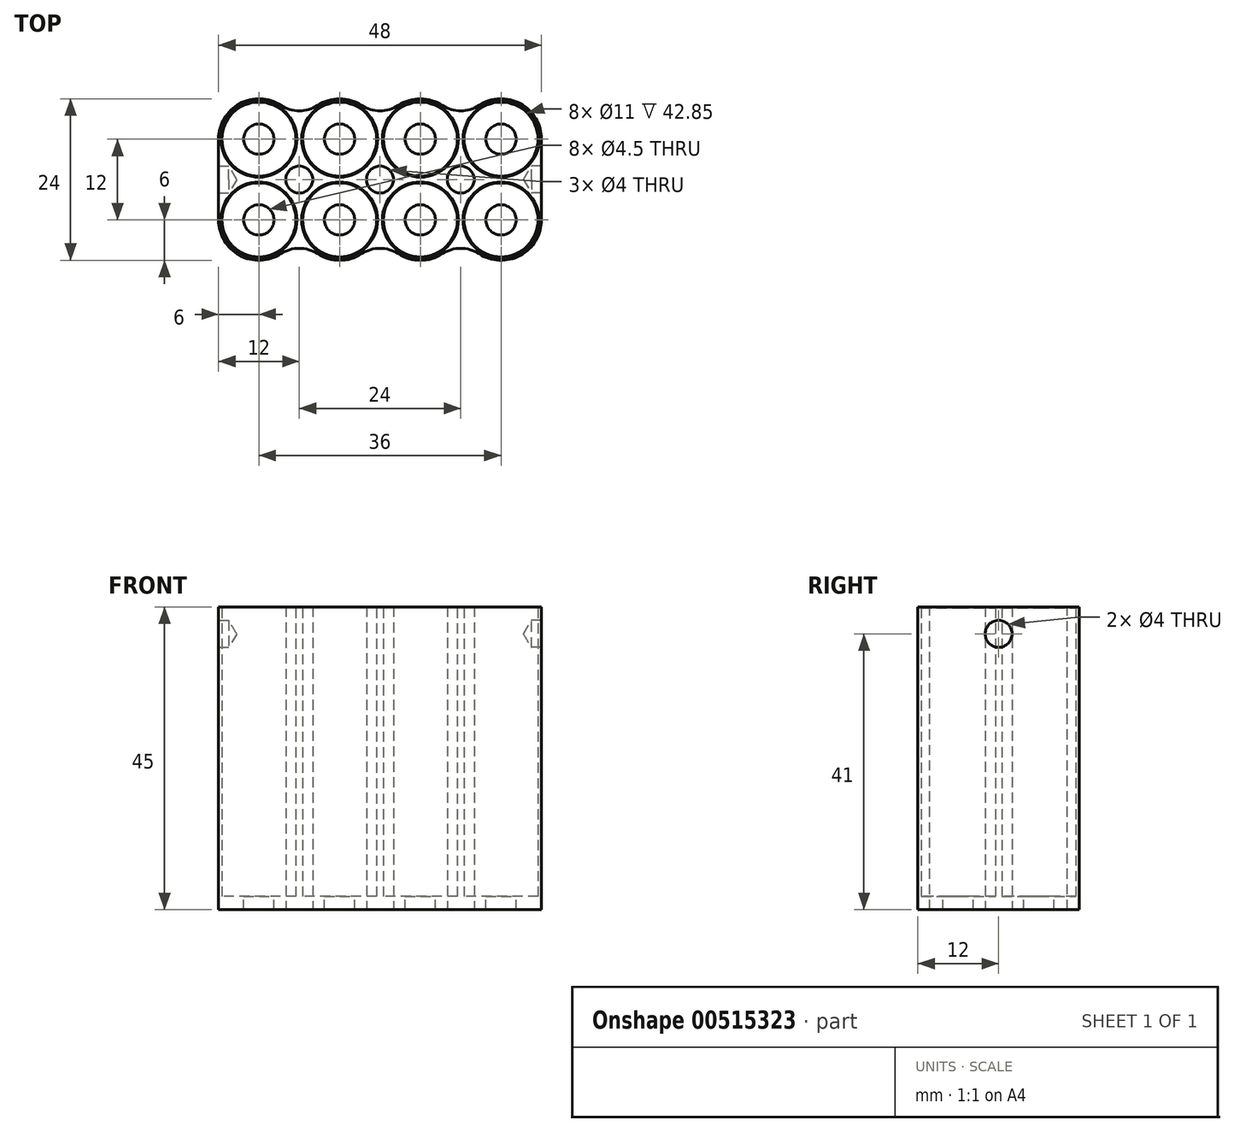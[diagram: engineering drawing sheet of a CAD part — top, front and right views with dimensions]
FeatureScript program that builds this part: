
annotation { "Feature Type Name" : "Feature", "Feature Type Description" : "" }
export const myFeature = defineFeature(function(context is Context, id is Id, definition is map)
    precondition{}
    {
        {
            var Q0;
            Q0=qCreatedBy(makeId("Top.planeOp"),FACE);
            var sketch = newSketch(context, id + "F0", { "sketchPlane" : qUnion([Q0])});
            skCircle(sketch, "E0", {"center": v(-6, 6) * mm, "radius": 5.5 * mm});
            skCircle(sketch, "E1", {"center": v(-18, 6) * mm, "radius": 5.5 * mm});
            skArc(sketch, "E2", {"start": v(-12, 6) * mm, "mid": v(-18, 12) * mm, "end": v(-24, 6) * mm});
            skArc(sketch, "E3", {"start": v(0, 6) * mm, "mid": v(-6, 12) * mm, "end": v(-12, 6) * mm});
            skCircle(sketch, "E4.MirrorC", {"center": v(-6, -6) * mm, "radius": 5.5 * mm});
            skCircle(sketch, "E5.MirrorC", {"center": v(-18, -6) * mm, "radius": 5.5 * mm});
            skArc(sketch, "E6.MirrorCS", {"start": v(0, -6) * mm, "mid": v(-6, -12) * mm, "end": v(-12, -6) * mm});
            skArc(sketch, "E7.MirrorCS", {"start": v(-12, -6) * mm, "mid": v(-18, -12) * mm, "end": v(-24, -6) * mm});
            skCircle(sketch, "E8.MirrorC", {"center": v(18, 6) * mm, "radius": 5.5 * mm});
            skCircle(sketch, "E9.MirrorC", {"center": v(6, -6) * mm, "radius": 5.5 * mm});
            skCircle(sketch, "E10.MirrorC", {"center": v(6, 6) * mm, "radius": 5.5 * mm});
            skArc(sketch, "E11.MirrorCS", {"start": v(0, -6) * mm, "mid": v(6, -12) * mm, "end": v(12, -6) * mm});
            skArc(sketch, "E12.MirrorCS", {"start": v(12, 6) * mm, "mid": v(18, 12) * mm, "end": v(24, 6) * mm});
            skArc(sketch, "E13.MirrorCS", {"start": v(12, -6) * mm, "mid": v(18, -12) * mm, "end": v(24, -6) * mm});
            skCircle(sketch, "E14.MirrorC", {"center": v(18, -6) * mm, "radius": 5.5 * mm});
            skArc(sketch, "E15.MirrorCS", {"start": v(0, 6) * mm, "mid": v(6, 12) * mm, "end": v(12, 6) * mm});
            skCircle(sketch, "E16", {"center": v(-12, 0) * mm, "radius": 2 * mm});
            skCircle(sketch, "E17", {"center": v(0, 0) * mm, "radius": 2 * mm});
            skCircle(sketch, "E18", {"center": v(12, 0) * mm, "radius": 2 * mm});
            skLineSegment(sketch, "E19", {"start": v(-24, 6) * mm, "end": v(-24, -6) * mm});
            skLineSegment(sketch, "E20", {"start": v(24, 6) * mm, "end": v(24, -6) * mm});
            skSolve(sketch);
        }
        {
            var Q0;
            Q0 = qSketchRegion(id + "F0", true);
            extrude(context, id + "F1", {"entities" : qUnion([Q0]), "depth" : 43 * mm, "offsetDistance" : 25 * mm});
        }
        {
            var Q0;
            Q0=makeQuery(id+"F1.opExtrude","CAP_FACE",FACE,{"disambiguationData":[OSD([sQuery(id+"F0.wireOp",EDGE,"E0"),sQuery(id+"F0.wireOp",EDGE,"E1"),sQuery(id+"F0.wireOp",EDGE,"E2"),sQuery(id+"F0.wireOp",EDGE,"E3"),sQuery(id+"F0.wireOp",EDGE,"E4.MirrorC"),sQuery(id+"F0.wireOp",EDGE,"E5.MirrorC"),sQuery(id+"F0.wireOp",EDGE,"E6.MirrorCS"),sQuery(id+"F0.wireOp",EDGE,"E7.MirrorCS"),sQuery(id+"F0.wireOp",EDGE,"E8.MirrorC"),sQuery(id+"F0.wireOp",EDGE,"E9.MirrorC"),sQuery(id+"F0.wireOp",EDGE,"E10.MirrorC"),sQuery(id+"F0.wireOp",EDGE,"E11.MirrorCS"),sQuery(id+"F0.wireOp",EDGE,"E12.MirrorCS"),sQuery(id+"F0.wireOp",EDGE,"E13.MirrorCS"),sQuery(id+"F0.wireOp",EDGE,"E14.MirrorC"),sQuery(id+"F0.wireOp",EDGE,"E15.MirrorCS"),sQuery(id+"F0.wireOp",EDGE,"2cUwnYCC-gtrQ-3R2t-ya3r-G7VDNndyc5e5"),sQuery(id+"F0.wireOp",EDGE,"hSRJbXHy-CsvW-6MMe-1okK-EmNHOIwR2LyR"),sQuery(id+"F0.wireOp",EDGE,"E16"),sQuery(id+"F0.wireOp",EDGE,"E17"),sQuery(id+"F0.wireOp",EDGE,"E18")])],"isStart":true});
            var sketch = newSketch(context, id + "F2", { "sketchPlane" : qUnion([Q0])});
            skArc(sketch, "E21", {"start": v(0, 6) * mm, "mid": v(-6, 12) * mm, "end": v(-12, 6) * mm});
            skArc(sketch, "E22", {"start": v(12, 6) * mm, "mid": v(6, 12) * mm, "end": v(0, 6) * mm});
            skArc(sketch, "E23", {"start": v(-12, -6) * mm, "mid": v(-6, -12) * mm, "end": v(0, -6) * mm});
            skArc(sketch, "E24", {"start": v(0, -6) * mm, "mid": v(6, -12) * mm, "end": v(12, -6) * mm});
            skCircle(sketch, "E25", {"center": v(-6, 6) * mm, "radius": 2.25 * mm});
            skCircle(sketch, "E26", {"center": v(6, 6) * mm, "radius": 2.25 * mm});
            skCircle(sketch, "E27", {"center": v(-6, -6) * mm, "radius": 2.25 * mm});
            skCircle(sketch, "E28", {"center": v(6, -6) * mm, "radius": 2.25 * mm});
            skCircle(sketch, "E29", {"center": v(0, 0) * mm, "radius": 2 * mm});
            skCircle(sketch, "E30", {"center": v(-12, 0) * mm, "radius": 2 * mm});
            skArc(sketch, "E31", {"start": v(12, -6) * mm, "mid": v(18, -12) * mm, "end": v(24, -6) * mm});
            skLineSegment(sketch, "E32", {"start": v(-12, 6) * mm, "end": v(-12, 6) * mm});
            skCircle(sketch, "E33", {"center": v(-18, 6) * mm, "radius": 2.25 * mm});
            skCircle(sketch, "E34", {"center": v(18, -6) * mm, "radius": 2.25 * mm});
            skLineSegment(sketch, "E35", {"start": v(24, -6) * mm, "end": v(24, 6) * mm});
            skArc(sketch, "E36", {"start": v(24, 6) * mm, "mid": v(18, 12) * mm, "end": v(12, 6) * mm});
            skArc(sketch, "E37", {"start": v(-24, -6) * mm, "mid": v(-18, -12) * mm, "end": v(-12, -6) * mm});
            skArc(sketch, "E38", {"start": v(-12, 6) * mm, "mid": v(-18, 12) * mm, "end": v(-24, 6) * mm});
            skLineSegment(sketch, "E39", {"start": v(-24, -6) * mm, "end": v(-24, 6) * mm});
            skCircle(sketch, "E40", {"center": v(-18, -6) * mm, "radius": 2.25 * mm});
            skCircle(sketch, "E41", {"center": v(18, 6) * mm, "radius": 2.25 * mm});
            skCircle(sketch, "E42", {"center": v(12, 0) * mm, "radius": 2 * mm});
            skSolve(sketch);
        }
        {
            var Q0;
            Q0=makeQuery(id+"F1.opExtrude","CAP_EDGE",EDGE,{"disambiguationData":[OSD([sQuery(id+"F0.wireOp",EDGE,"E1")])],"isStart":false});
            var Q1;
            Q1=makeQuery(id+"F1.opExtrude","CAP_EDGE",EDGE,{"disambiguationData":[OSD([sQuery(id+"F0.wireOp",EDGE,"E0")])],"isStart":false});
            var Q2;
            Q2=makeQuery(id+"F1.opExtrude","CAP_EDGE",EDGE,{"disambiguationData":[OSD([sQuery(id+"F0.wireOp",EDGE,"E10.MirrorC")])],"isStart":false});
            var Q3;
            Q3=makeQuery(id+"F1.opExtrude","CAP_EDGE",EDGE,{"disambiguationData":[OSD([sQuery(id+"F0.wireOp",EDGE,"E8.MirrorC")])],"isStart":false});
            var Q4;
            Q4=makeQuery(id+"F1.opExtrude","CAP_EDGE",EDGE,{"disambiguationData":[OSD([sQuery(id+"F0.wireOp",EDGE,"E14.MirrorC")])],"isStart":false});
            var Q5;
            Q5=makeQuery(id+"F1.opExtrude","CAP_EDGE",EDGE,{"disambiguationData":[OSD([sQuery(id+"F0.wireOp",EDGE,"E9.MirrorC")])],"isStart":false});
            var Q6;
            Q6=makeQuery(id+"F1.opExtrude","CAP_EDGE",EDGE,{"disambiguationData":[OSD([sQuery(id+"F0.wireOp",EDGE,"E4.MirrorC")])],"isStart":false});
            var Q7;
            Q7=makeQuery(id+"F1.opExtrude","CAP_EDGE",EDGE,{"disambiguationData":[OSD([sQuery(id+"F0.wireOp",EDGE,"E5.MirrorC")])],"isStart":false});
            chamfer(context, id + "F3", {"entities" : qUnion([Q0, Q1, Q2, Q3, Q4, Q5, Q6, Q7]), "width" : .15 * mm, "tangentPropagation" : true});
        }
        {
            var Q0;
            Q0=makeQuery(id+"F1.opExtrude","SWEPT_FACE",FACE,{"disambiguationData":[OSD([sQuery(id+"F0.wireOp",EDGE,"E19")])]});
            var sketch = newSketch(context, id + "F4", { "sketchPlane" : qUnion([Q0])});
            skPoint(sketch, "E43", {"position": v(0, 39) * mm});
            skSolve(sketch);
        }
        {
            var Q0;
            Q0 = qSketchRegion(id + "F2", true);
            extrude(context, id + "F5", {"entities" : qUnion([Q0]), "operationType" : NewBodyOperationType.ADD, "depth" : 2 * mm, "offsetDistance" : 25 * mm});
        }
        {
            var Q0;
            Q0=makeQuery(id+"F5.boolean.opBoolean","MERGE",EDGE,{"derivedFrom":[makeQuery(id+"F1.opExtrude","SWEPT_EDGE",EDGE,{"disambiguationData":[OSD([sQuery(id+"F0.wireOp",EDGE,"E11.MirrorCS"),sQuery(id+"F0.wireOp",EDGE,"E13.MirrorCS")])]}),makeQuery(id+"F5.opExtrude","SWEPT_EDGE",EDGE,{"disambiguationData":[OSD([sQuery(id+"F2.wireOp",EDGE,"E22"),sQuery(id+"F2.wireOp",EDGE,"E36")])]})]});
            var Q1;
            Q1=makeQuery(id+"F5.boolean.opBoolean","MERGE",EDGE,{"derivedFrom":[makeQuery(id+"F1.opExtrude","SWEPT_EDGE",EDGE,{"disambiguationData":[OSD([sQuery(id+"F0.wireOp",EDGE,"E6.MirrorCS"),sQuery(id+"F0.wireOp",EDGE,"E11.MirrorCS")])]}),makeQuery(id+"F5.opExtrude","SWEPT_EDGE",EDGE,{"disambiguationData":[OSD([sQuery(id+"F2.wireOp",EDGE,"E21"),sQuery(id+"F2.wireOp",EDGE,"E22")])]})]});
            var Q2;
            Q2=makeQuery(id+"F5.boolean.opBoolean","MERGE",EDGE,{"derivedFrom":[makeQuery(id+"F1.opExtrude","SWEPT_EDGE",EDGE,{"disambiguationData":[OSD([sQuery(id+"F0.wireOp",EDGE,"E6.MirrorCS"),sQuery(id+"F0.wireOp",EDGE,"E7.MirrorCS")])]}),makeQuery(id+"F5.opExtrude","SWEPT_EDGE",EDGE,{"disambiguationData":[OSD([sQuery(id+"F2.wireOp",EDGE,"E21"),sQuery(id+"F2.wireOp",EDGE,"E38")])]})]});
            var Q3;
            Q3=makeQuery(id+"F5.boolean.opBoolean","MERGE",EDGE,{"derivedFrom":[makeQuery(id+"F1.opExtrude","SWEPT_EDGE",EDGE,{"disambiguationData":[OSD([sQuery(id+"F0.wireOp",EDGE,"E12.MirrorCS"),sQuery(id+"F0.wireOp",EDGE,"E15.MirrorCS")])]}),makeQuery(id+"F5.opExtrude","SWEPT_EDGE",EDGE,{"disambiguationData":[OSD([sQuery(id+"F2.wireOp",EDGE,"E24"),sQuery(id+"F2.wireOp",EDGE,"E31")])]})]});
            var Q4;
            Q4=makeQuery(id+"F5.boolean.opBoolean","MERGE",EDGE,{"derivedFrom":[makeQuery(id+"F1.opExtrude","SWEPT_EDGE",EDGE,{"disambiguationData":[OSD([sQuery(id+"F0.wireOp",EDGE,"E3"),sQuery(id+"F0.wireOp",EDGE,"E15.MirrorCS")])]}),makeQuery(id+"F5.opExtrude","SWEPT_EDGE",EDGE,{"disambiguationData":[OSD([sQuery(id+"F2.wireOp",EDGE,"E23"),sQuery(id+"F2.wireOp",EDGE,"E24")])]})]});
            var Q5;
            Q5=makeQuery(id+"F5.boolean.opBoolean","MERGE",EDGE,{"derivedFrom":[makeQuery(id+"F1.opExtrude","SWEPT_EDGE",EDGE,{"disambiguationData":[OSD([sQuery(id+"F0.wireOp",EDGE,"E2"),sQuery(id+"F0.wireOp",EDGE,"E3")])]}),makeQuery(id+"F5.opExtrude","SWEPT_EDGE",EDGE,{"disambiguationData":[OSD([sQuery(id+"F2.wireOp",EDGE,"E23"),sQuery(id+"F2.wireOp",EDGE,"E37")])]})]});
            fillet(context, id + "F6", {"entities" : qUnion([Q0, Q1, Q2, Q3, Q4, Q5]), "radius" : 5 * mm, "tangentPropagation" : true, "allowEdgeOverflow" : false});
        }
        {
            var Q0;
            Q0=makeQuery(id+"F5.boolean.opBoolean","MERGE",FACE,{"derivedFrom":[makeQuery(id+"F1.opExtrude","SWEPT_FACE",FACE,{"disambiguationData":[OSD([sQuery(id+"F0.wireOp",EDGE,"E20")])]}),makeQuery(id+"F5.opExtrude","SWEPT_FACE",FACE,{"disambiguationData":[OSD([sQuery(id+"F2.wireOp",EDGE,"E35")])]})]});
            var sketch = newSketch(context, id + "F7", { "sketchPlane" : qUnion([Q0])});
            skPoint(sketch, "E44", {"position": v(0, 39) * mm});
            skSolve(sketch);
        }
        {
            var Q0;
            Q0=sQuery(id+"F7.wireOp",VERTEX,"E44");
            var Q1;
            Q1=sQuery(id+"F4.wireOp",VERTEX,"E43");
            var Q2;
            Q2=makeQuery(id+"F1.opExtrude","SWEPT_BODY",BODY,{"disambiguationData":[OSD([sQuery(id+"F0.wireOp",EDGE,"E0"),sQuery(id+"F0.wireOp",EDGE,"E1"),sQuery(id+"F0.wireOp",EDGE,"E2"),sQuery(id+"F0.wireOp",EDGE,"E3"),sQuery(id+"F0.wireOp",EDGE,"E4.MirrorC"),sQuery(id+"F0.wireOp",EDGE,"E5.MirrorC"),sQuery(id+"F0.wireOp",EDGE,"E6.MirrorCS"),sQuery(id+"F0.wireOp",EDGE,"E7.MirrorCS"),sQuery(id+"F0.wireOp",EDGE,"E8.MirrorC"),sQuery(id+"F0.wireOp",EDGE,"E9.MirrorC"),sQuery(id+"F0.wireOp",EDGE,"E10.MirrorC"),sQuery(id+"F0.wireOp",EDGE,"E11.MirrorCS"),sQuery(id+"F0.wireOp",EDGE,"E12.MirrorCS"),sQuery(id+"F0.wireOp",EDGE,"E13.MirrorCS"),sQuery(id+"F0.wireOp",EDGE,"E14.MirrorC"),sQuery(id+"F0.wireOp",EDGE,"E15.MirrorCS"),sQuery(id+"F0.wireOp",EDGE,"E16"),sQuery(id+"F0.wireOp",EDGE,"E17"),sQuery(id+"F0.wireOp",EDGE,"E18"),sQuery(id+"F0.wireOp",EDGE,"E19"),sQuery(id+"F0.wireOp",EDGE,"E20")])]});
            hole(context, id + "F8", {"style" : HoleStyle.SIMPLE, "endStyle" : HoleEndStyle.BLIND, "holeDiameter" : 4 * mm, "holeDepth" : 1.5 * mm, "isTappedThrough" : true, "tappedDepth" : 12 * mm, "tapClearance" : 3, "locations" : qUnion([Q0, Q1]), "scope" : qUnion([Q2]), "startStyle" : HoleStartStyle.SKETCH});
        }
    });
